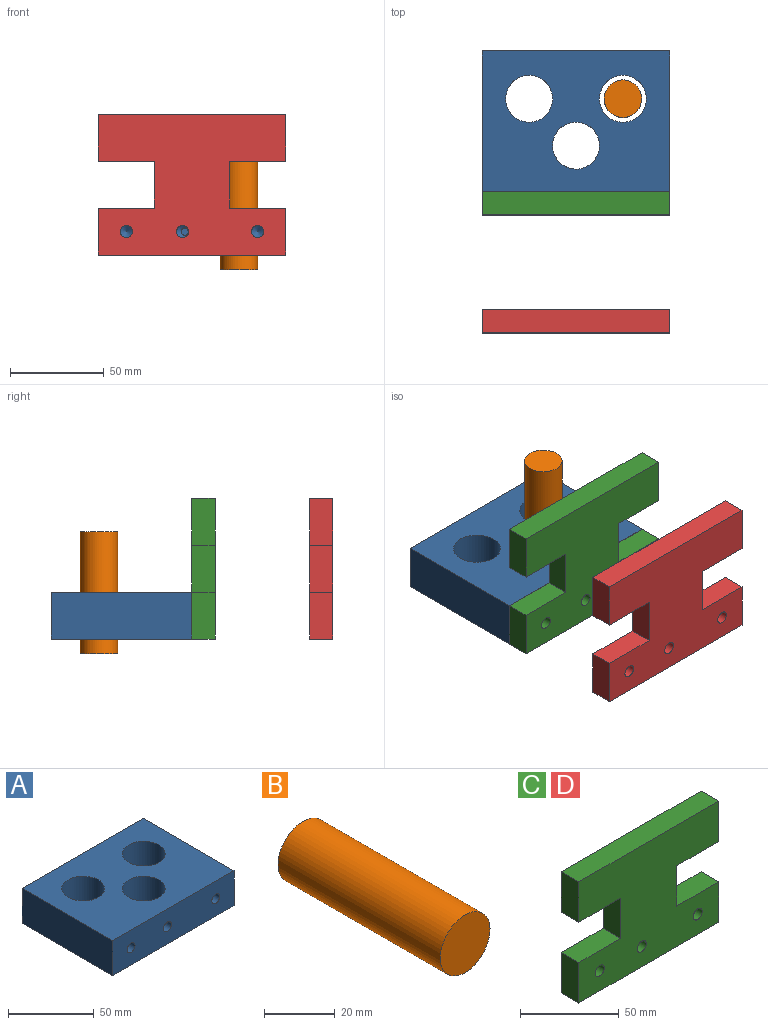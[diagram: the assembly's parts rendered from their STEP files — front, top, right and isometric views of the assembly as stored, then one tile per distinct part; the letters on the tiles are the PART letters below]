
ASSEMBLY  parts=4 mates=4
PART A: 15 faces, bbox 100x75x25 mm
  f0: cylinder r=12.5mm len=25mm, axis (0,0,1), area 1951.1mm2, adj f5,f6,f9
  f1: plane 75x25mm, normal (-1,0,0), area 1875mm2, adj f2,f4,f5,f6
  f2: plane 100x25mm, normal (0,-1,0), area 2397.4mm2, adj f1,f3,f5,f6,f10,f12,f14
  f3: plane 75x25mm, normal (1,0,0), area 1875mm2, adj f2,f4,f5,f6
  f4: plane 100x25mm, normal (0,1,0), area 2500mm2, adj f1,f3,f5,f6
  f5: plane 100x75mm, normal (0,0,1), area 6027.4mm2, adj f0,f1,f2,f3,f4,f7,f8
  f6: plane 100x75mm, normal (0,0,-1), area 6027.4mm2, adj f0,f1,f2,f3,f4,f7,f8
  f7: cylinder r=12.5mm len=25mm, axis (0,0,1), area 1963.5mm2, adj f5,f6
  f8: cylinder r=12.5mm len=25mm, axis (0,0,1), area 1963.5mm2, adj f5,f6
  f9: cone r=0mm half-angle=59deg, axis (0,-1,0), area 26.2mm2, adj f0,f10
  f10: cylinder r=3.3mm len=12mm, axis (0,-1,0), area 248.8mm2, adj f2,f9
  f11: cone r=0mm half-angle=59deg, axis (0,-1,0), area 39.9mm2, adj f12
  f12: cylinder r=3.3mm len=12mm, axis (0,-1,0), area 248.8mm2, adj f2,f11
  f13: cone r=0mm half-angle=59deg, axis (0,-1,0), area 39.9mm2, adj f14
  f14: cylinder r=3.3mm len=12mm, axis (0,-1,0), area 248.8mm2, adj f2,f13
PART B: 3 faces, bbox 20x65x20 mm
  f0: cylinder r=10mm len=65mm, axis (0,1,0), area 4084.1mm2, adj f1,f2
  f1: plane 20x20mm, normal (0,-1,0), area 314.2mm2, adj f0
  f2: plane 20x20mm, normal (0,1,0), area 314.2mm2, adj f0
PART C: 17 faces, bbox 100x12.5x75 mm
  f0: plane 25x12.5mm, normal (-1,0,0), area 312.5mm2, adj f1,f13,f15,f16
  f1: plane 100x12.5mm, normal (0,0,-1), area 1250mm2, adj f0,f2,f15,f16
  f2: plane 25x12.5mm, normal (1,0,0), area 312.5mm2, adj f1,f3,f15,f16
  f3: plane 30x12.5mm, normal (0,0,1), area 375mm2, adj f2,f4,f15,f16
  f4: plane 25x12.5mm, normal (1,0,0), area 312.5mm2, adj f3,f5,f15,f16
  f5: plane 30x12.5mm, normal (0,0,-1), area 375mm2, adj f4,f6,f15,f16
  f6: plane 25x12.5mm, normal (1,0,0), area 312.5mm2, adj f5,f7,f15,f16
  f7: plane 100x12.5mm, normal (0,0,1), area 1250mm2, adj f6,f8,f15,f16
  f8: plane 25x12.5mm, normal (-1,0,0), area 312.5mm2, adj f7,f9,f15,f16
  f9: plane 30x12.5mm, normal (0,0,-1), area 375mm2, adj f8,f10,f15,f16
  f10: plane 25x12.5mm, normal (-1,0,0), area 312.5mm2, adj f9,f13,f15,f16
  f11: cylinder r=3.25mm len=12.5mm, axis (0,1,0), area 255.3mm2, adj f15,f16
  f12: cylinder r=3.25mm len=12.5mm, axis (0,1,0), area 255.3mm2, adj f15,f16
  f13: plane 30x12.5mm, normal (0,0,1), area 375mm2, adj f0,f10,f15,f16
  f14: cylinder r=3.25mm len=12.5mm, axis (0,1,0), area 255.3mm2, adj f15,f16
  f15: plane 100x75mm, normal (0,-1,0), area 5900.5mm2, adj f0,f1,f2,f3,f4,f5,f6,f7
  f16: plane 100x75mm, normal (0,1,0), area 5900.5mm2, adj f0,f1,f2,f3,f4,f5,f6,f7
PART D: same geometry as C
PLACE A t=(35.91,-31.67,-28.67)mm
PLACE B rot(axis=(1,0,0),90deg) t=(110.91,17.85,28.58)mm
PLACE C t=(35.91,-31.67,-28.67)mm
PLACE D t=(35.91,-94.51,-28.67)mm
MATE parallel C.f16 <-> A.f13  axis (0,1,0) through (85.94,-31.67,9.26)mm
MATE slider B.f0 <-> A.f8  axis (0,0,1) through (110.91,17.85,28.58)mm
MATE slider D.f12 <-> C.f12  axis (0,-1,0) through (50.91,-107.01,-16.17)mm
MATE fastened C.f11 <-> A.f9  axis (0,1,0) through (80.91,-31.67,-16.17)mm
